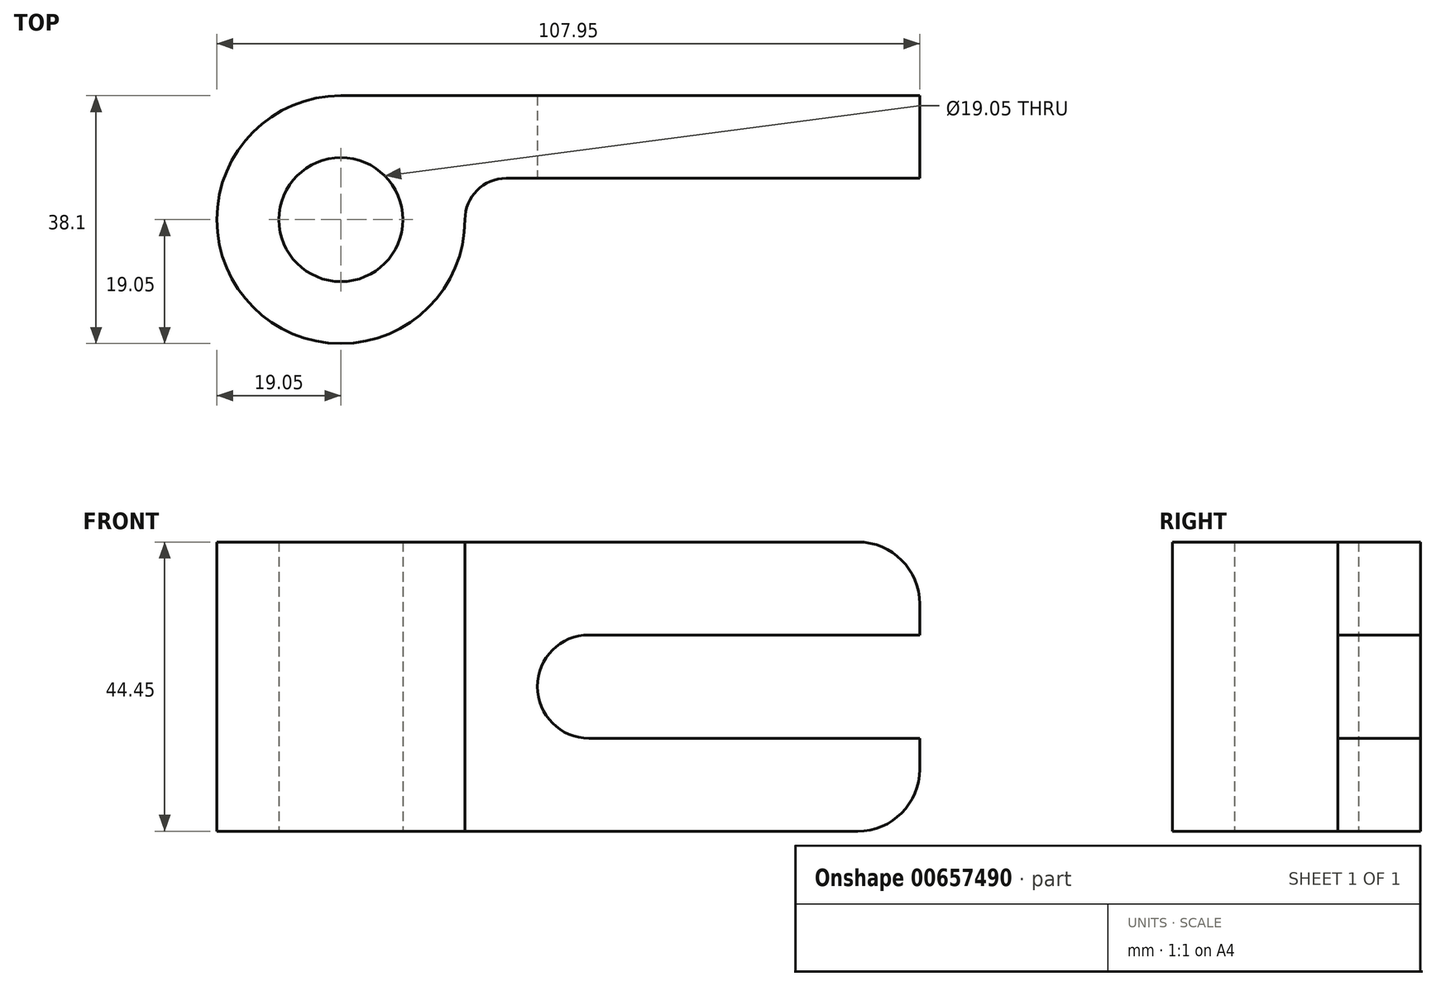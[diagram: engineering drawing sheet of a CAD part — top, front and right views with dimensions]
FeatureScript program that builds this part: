
annotation { "Feature Type Name" : "Feature", "Feature Type Description" : "" }
export const myFeature = defineFeature(function(context is Context, id is Id, definition is map)
    precondition{}
    {
        {
            var Q0;
            Q0=qCreatedBy(makeId("Top.planeOp"),FACE);
            var sketch = newSketch(context, id + "F0", { "sketchPlane" : qUnion([Q0])});
            skCircle(sketch, "E0", {"center": v(0, 0) * mm, "radius": 9.53 * mm});
            skArc(sketch, "E1", {"start": v(17.96, 6.35) * mm, "mid": v(-18.78, -3.22) * mm, "end": v(19.05, 0) * mm});
            skLineSegment(sketch, "E2", {"start": v(0, 19.05) * mm, "end": v(38.1, 19.05) * mm});
            skLineSegment(sketch, "E3", {"start": v(38.1, 19.05) * mm, "end": v(88.9, 19.05) * mm});
            skLineSegment(sketch, "E4", {"start": v(88.9, 19.05) * mm, "end": v(88.9, 6.35) * mm});
            skLineSegment(sketch, "E5", {"start": v(88.9, 6.35) * mm, "end": v(38.1, 6.35) * mm});
            skLineSegment(sketch, "E6", {"start": v(38.1, 6.35) * mm, "end": v(17.96, 6.35) * mm});
            skLineSegment(sketch, "E7", {"start": v(0, 0) * mm, "end": v(19.05, 0) * mm});
            skLineSegment(sketch, "E8", {"start": v(19.05, 0) * mm, "end": v(19.05, 6.35) * mm});
            skSolve(sketch);
        }
        {
            var Q0;
            Q0 = qSketchRegion(id + "F0", true);
            extrude(context, id + "F1", {"entities" : qUnion([Q0]), "depth" : 44.45 * mm, "offsetDistance" : 25.4 * mm});
        }
        {
            var Q0;
            Q0=makeQuery(id+"F1.opExtrude","SWEPT_EDGE",EDGE,{"disambiguationData":[OSD([sQuery(id+"F0.wireOp",EDGE,"E6"),sQuery(id+"F0.wireOp",EDGE,"E8")])]});
            fillet(context, id + "F2", {"entities" : qUnion([Q0]), "radius" : 6.35 * mm, "tangentPropagation" : true, "allowEdgeOverflow" : false});
        }
        {
            var Q0;
            Q0=makeQuery(id+"F1.opExtrude","SWEPT_FACE",FACE,{"disambiguationData":[OSD([sQuery(id+"F0.wireOp",EDGE,"E5"),sQuery(id+"F0.wireOp",EDGE,"E6")])]});
            var sketch = newSketch(context, id + "F3", { "sketchPlane" : qUnion([Q0])});
            skLineSegment(sketch, "E9", {"start": v(88.9, 44.45) * mm, "end": v(88.9, 30.16) * mm});
            skLineSegment(sketch, "E10", {"start": v(88.9, 30.16) * mm, "end": v(88.9, 14.29) * mm});
            skLineSegment(sketch, "E11", {"start": v(88.9, 14.29) * mm, "end": v(88.9, 0) * mm});
            skLineSegment(sketch, "E12", {"start": v(88.9, 14.29) * mm, "end": v(38.1, 14.29) * mm});
            skLineSegment(sketch, "E13", {"start": v(88.9, 30.16) * mm, "end": v(38.1, 30.16) * mm});
            skLineSegment(sketch, "E14", {"start": v(38.1, 30.16) * mm, "end": v(38.1, 14.29) * mm});
            skLineSegment(sketch, "E15", {"start": v(38.1, 30.16) * mm, "end": v(38.1, 22.23) * mm});
            skCircle(sketch, "E16", {"center": v(38.1, 22.23) * mm, "radius": 7.94 * mm});
            skSolve(sketch);
        }
        {
            var Q0;
            Q0 = qSketchRegion(id + "F3", true);
            extrude(context, id + "F4", {"entities" : qUnion([Q0]), "operationType" : NewBodyOperationType.REMOVE, "oppositeDirection" : true, "depth" : 12.7 * mm, "offsetDistance" : 25.4 * mm});
        }
        {
            var Q0;
            Q0=makeQuery(id+"F1.opExtrude","CAP_EDGE",EDGE,{"disambiguationData":[OSD([sQuery(id+"F0.wireOp",EDGE,"E4")])],"isStart":false});
            var Q1;
            Q1=makeQuery(id+"F1.opExtrude","CAP_EDGE",EDGE,{"disambiguationData":[OSD([sQuery(id+"F0.wireOp",EDGE,"E4")])],"isStart":true});
            fillet(context, id + "F5", {"entities" : qUnion([Q0, Q1]), "radius" : 9.52 * mm, "tangentPropagation" : true, "allowEdgeOverflow" : false});
        }
    });
